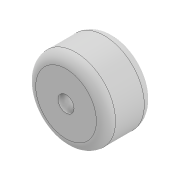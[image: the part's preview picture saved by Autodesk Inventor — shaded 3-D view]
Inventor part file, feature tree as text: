
AUTODESK INVENTOR PART (.ipt)
format: ipt  version: 2020 (Build 240168000, 168)  size: 120,832 bytes
history: native  units: mm
features: other x1, extrude x1, fillet x1, sketch x1
ambient origin geometry x8: Origin, YZ Plane, XZ Plane, XY Plane, X Axis, Y Axis, Z Axis, Center Point
bodies: Body1 (feature_tree)
feature tree (4):
  other  "솔리드1"
  extrude  "돌출1"  Depth=25.0mm
  fillet  "모깎기1"  Radius=5.0mm
  sketch  "스케치1"
